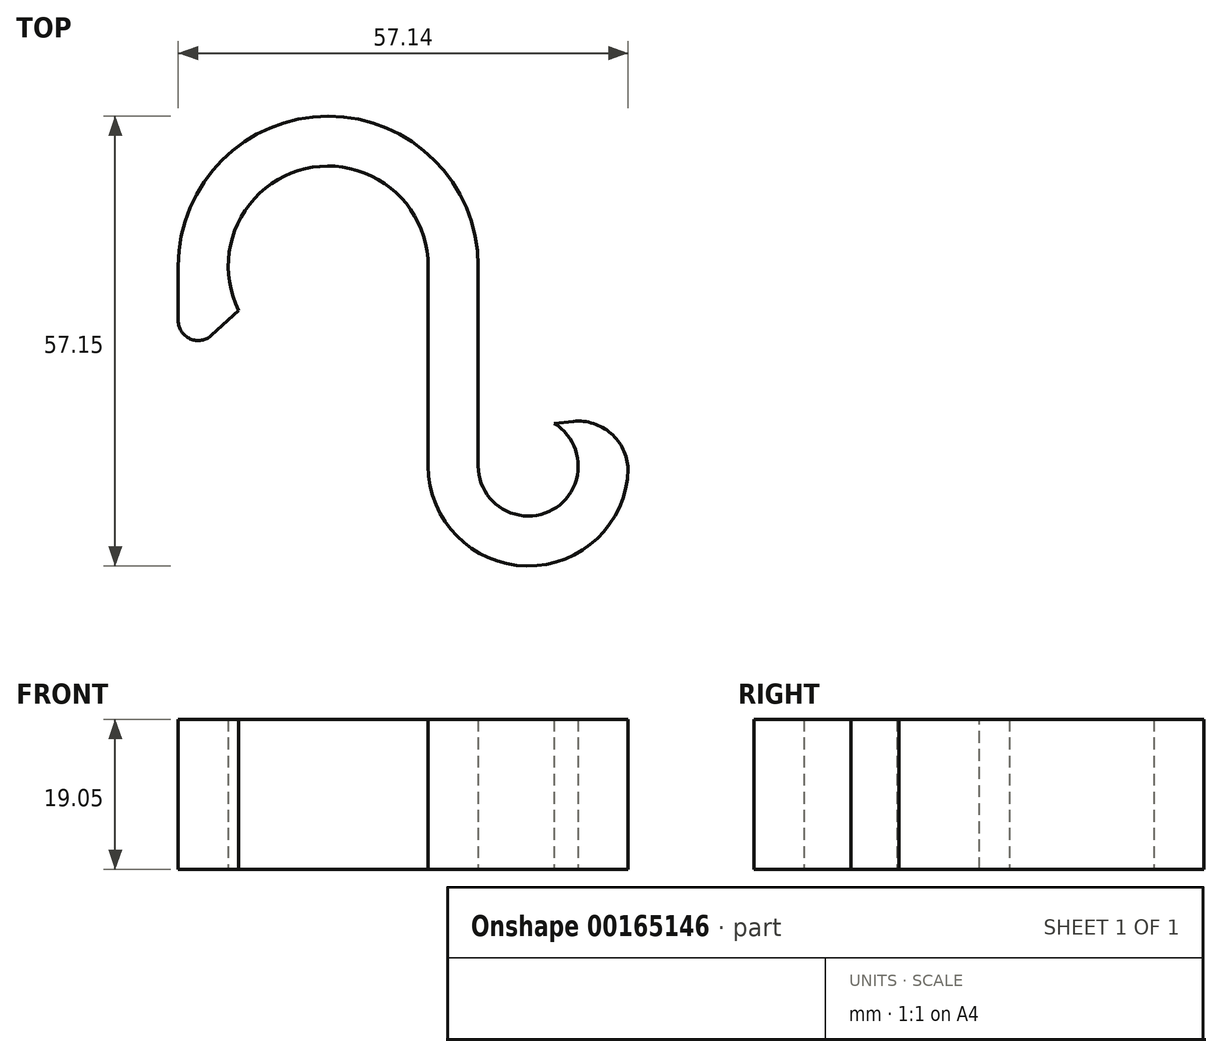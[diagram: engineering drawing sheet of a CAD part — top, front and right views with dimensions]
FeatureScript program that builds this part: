
annotation { "Feature Type Name" : "Feature", "Feature Type Description" : "" }
export const myFeature = defineFeature(function(context is Context, id is Id, definition is map)
    precondition{}
    {
        {
            var Q0;
            Q0=qCreatedBy(makeId("Top.planeOp"),FACE);
            var sketch = newSketch(context, id + "F0", { "sketchPlane" : qUnion([Q0])});
            skLineSegment(sketch, "E0.bottom", {"start": v(-25.4, 9.5) * mm, "end": v(-19.05, 9.5) * mm});
            skLineSegment(sketch, "E0.top", {"start": v(-25.4, -15.9) * mm, "end": v(-19.05, -15.9) * mm});
            skLineSegment(sketch, "E0.left", {"start": v(-25.4, 9.5) * mm, "end": v(-25.4, -15.9) * mm});
            skLineSegment(sketch, "E0.right", {"start": v(-19.05, 9.5) * mm, "end": v(-19.05, -15.9) * mm});
            skArc(sketch, "E1", {"start": v(-25.4, 9.5) * mm, "mid": v(-38.1, 22.2) * mm, "end": v(-50.8, 9.5) * mm});
            skArc(sketch, "E2", {"start": v(-19.05, 9.5) * mm, "mid": v(-38.1, 28.56) * mm, "end": v(-57.15, 9.5) * mm});
            skArc(sketch, "E3", {"start": v(-19.05, -15.9) * mm, "mid": v(-12.7, -22.24) * mm, "end": v(-6.35, -15.9) * mm});
            skPoint(sketch, "E4.endSnap0", {"position": v(-22.23, -15.9) * mm});
            skPoint(sketch, "E5", {"position": v(5.9, -15.77) * mm});
            skLineSegment(sketch, "E6.right", {"start": v(-57.15, 9.5) * mm, "end": v(-57.15, -3.2) * mm});
            skPoint(sketch, "E6.top.start.orphan", {"position": v(-50.8, -3.2) * mm});
            skArc(sketch, "E7", {"start": v(-25.4, -15.9) * mm, "mid": v(-12.7, -28.6) * mm, "end": v(0, -15.9) * mm});
            skLineSegment(sketch, "E8", {"start": v(0, -16.54) * mm, "end": v(0, -15.9) * mm});
            skArc(sketch, "E9", {"start": v(-50.8, 9.5) * mm, "mid": v(-50.46, 6.6) * mm, "end": v(-49.47, 3.85) * mm});
            skLineSegment(sketch, "E10", {"start": v(-49.47, 3.85) * mm, "end": v(-57.15, -3.2) * mm});
            skArc(sketch, "E11", {"start": v(-6.35, -15.9) * mm, "mid": v(-7.17, -12.78) * mm, "end": v(-9.41, -10.46) * mm});
            skLineSegment(sketch, "E12", {"start": v(-9.41, -10.46) * mm, "end": v(-6.97, -10.22) * mm});
            skPoint(sketch, "E13.visualSharp", {"position": v(0, -9.54) * mm});
            skArc(sketch, "E13.filletArc", {"start": v(0, -16.54) * mm, "mid": v(-2.08, -11.84) * mm, "end": v(-6.97, -10.22) * mm});
            skSolve(sketch);
        }
        {
            var Q0;
            Q0=makeQuery(id+"F0.imprint","IMPRINT",FACE,{"disambiguationData":[TD([[makeQuery(id+"F0.imprint","IMPRINT",EDGE,{"derivedFrom":sQuery(id+"F0.wireOp",EDGE,"E0.bottom")}),1.0]])]});
            var Q1;
            Q1=makeQuery(id+"F0.imprint","IMPRINT",FACE,{"disambiguationData":[TD([[makeQuery(id+"F0.imprint","IMPRINT",EDGE,{"derivedFrom":sQuery(id+"F0.wireOp",EDGE,"E0.bottom")}),-1.0]])]});
            var Q2;
            Q2=makeQuery(id+"F0.imprint","IMPRINT",FACE,{"disambiguationData":[TD([[makeQuery(id+"F0.imprint","IMPRINT",EDGE,{"derivedFrom":sQuery(id+"F0.wireOp",EDGE,"E0.top")}),-1.0]])]});
            extrude(context, id + "F1", {"entities" : qUnion([Q0, Q1, Q2]), "depth" : 19.05 * mm});
        }
        {
            var Q0;
            Q0=makeQuery(id+"F1.opExtrude","SWEPT_EDGE",EDGE,{"disambiguationData":[OSD([sQuery(id+"F0.wireOp",EDGE,"E6.right"),sQuery(id+"F0.wireOp",EDGE,"E10")])]});
            fillet(context, id + "F2", {"entities" : qUnion([Q0]), "radius" : 2.54 * mm, "tangentPropagation" : true, "allowEdgeOverflow" : false});
        }
    });
